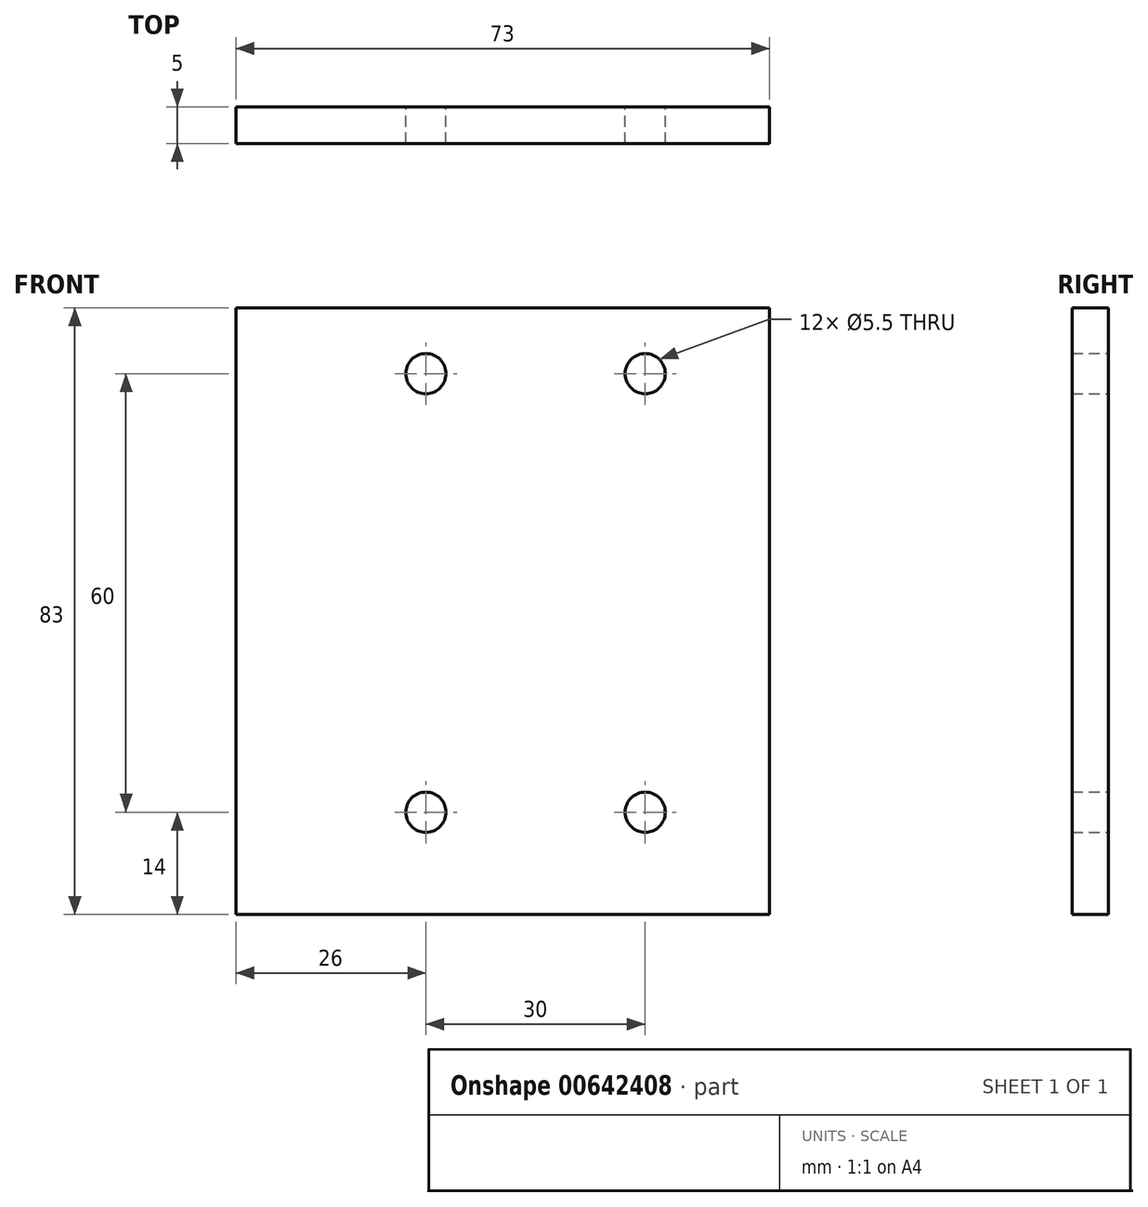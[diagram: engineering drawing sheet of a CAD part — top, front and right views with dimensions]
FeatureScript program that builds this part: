
annotation { "Feature Type Name" : "Feature", "Feature Type Description" : "" }
export const myFeature = defineFeature(function(context is Context, id is Id, definition is map)
    precondition{}
    {
        {
            var Q0;
            Q0=qCreatedBy(makeId("Front.planeOp"),FACE);
            var sketch = newSketch(context, id + "F0", { "sketchPlane" : qUnion([Q0])});
            skLineSegment(sketch, "E0.bottom", {"start": v(0, 0) * mm, "end": v(73, 0) * mm});
            skLineSegment(sketch, "E0.top", {"start": v(0, 83) * mm, "end": v(73, 83) * mm});
            skLineSegment(sketch, "E0.left", {"start": v(0, 0) * mm, "end": v(0, 83) * mm});
            skLineSegment(sketch, "E0.right", {"start": v(73, 0) * mm, "end": v(73, 83) * mm});
            skCircle(sketch, "E1", {"center": v(56, 74) * mm, "radius": 2.75 * mm});
            skCircle(sketch, "E2.0.1.0", {"center": v(56, 14) * mm, "radius": 2.75 * mm});
            skCircle(sketch, "E2.1.0.0", {"center": v(26, 74) * mm, "radius": 2.75 * mm});
            skCircle(sketch, "E2.1.1.0", {"center": v(26, 14) * mm, "radius": 2.75 * mm});
            skLineSegment(sketch, "E2.direction1", {"start": v(56, 74) * mm, "end": v(26, 74) * mm, "construction": true});
            skLineSegment(sketch, "E2.direction2", {"start": v(56, 74) * mm, "end": v(56, 14) * mm, "construction": true});
            skSolve(sketch);
        }
        {
            var Q0;
            Q0=makeQuery(id+"F0.imprint","IMPRINT",FACE,{"disambiguationData":[TD([[makeQuery(id+"F0.imprint","IMPRINT",EDGE,{"derivedFrom":sQuery(id+"F0.wireOp",EDGE,"E0.bottom")}),1.0]])]});
            extrude(context, id + "F1", {"entities" : qUnion([Q0]), "depth" : 5 * mm, "offsetDistance" : 25 * mm});
        }
    });
